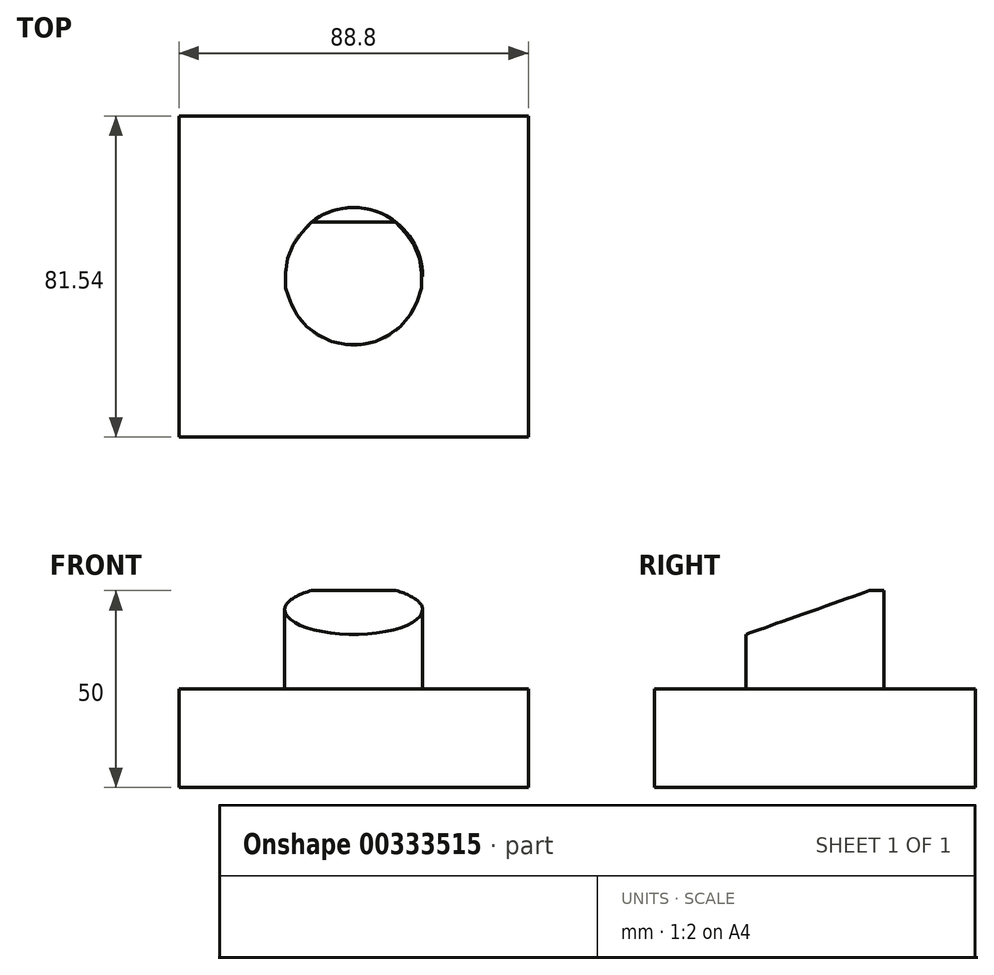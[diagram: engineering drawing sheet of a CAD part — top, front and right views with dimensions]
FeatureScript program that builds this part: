
annotation { "Feature Type Name" : "Feature", "Feature Type Description" : "" }
export const myFeature = defineFeature(function(context is Context, id is Id, definition is map)
    precondition{}
    {
        {
            var Q0;
            Q0=qCreatedBy(makeId("Top.planeOp"),FACE);
            var sketch = newSketch(context, id + "F0", { "sketchPlane" : qUnion([Q0])});
            skLineSegment(sketch, "E0.bottom", {"start": v(-52.21, -36.92) * mm, "end": v(52.21, -36.92) * mm});
            skLineSegment(sketch, "E0.top", {"start": v(-52.21, 36.92) * mm, "end": v(52.21, 36.92) * mm});
            skLineSegment(sketch, "E0.left", {"start": v(-52.21, -36.92) * mm, "end": v(-52.21, 36.92) * mm});
            skLineSegment(sketch, "E0.right", {"start": v(52.21, -36.92) * mm, "end": v(52.21, 36.92) * mm});
            skPoint(sketch, "E0.middle", {"position": v(0, 0) * mm});
            skCircle(sketch, "E1", {"center": v(0, 0) * mm, "radius": 17.54 * mm});
            skSolve(sketch);
        }
        {
            var Q0;
            Q0=makeQuery(id+"F0.imprint","IMPRINT",FACE,{"disambiguationData":[TD([[makeQuery(id+"F0.imprint","IMPRINT",EDGE,{"derivedFrom":sQuery(id+"F0.wireOp",EDGE,"E1")}),1.0]])]});
            extrude(context, id + "F1", {"entities" : qUnion([Q0]), "depth" : 50 * mm, "offsetDistance" : 25 * mm});
        }
        {
            var Q0;
            Q0=qCreatedBy(makeId("Top.planeOp"),FACE);
            var sketch = newSketch(context, id + "F2", { "sketchPlane" : qUnion([Q0])});
            skLineSegment(sketch, "E2.bottom", {"start": v(-44.4, -40.77) * mm, "end": v(44.4, -40.77) * mm});
            skLineSegment(sketch, "E2.top", {"start": v(-44.4, 40.77) * mm, "end": v(44.4, 40.77) * mm});
            skLineSegment(sketch, "E2.left", {"start": v(-44.4, -40.77) * mm, "end": v(-44.4, 40.77) * mm});
            skLineSegment(sketch, "E2.right", {"start": v(44.4, -40.77) * mm, "end": v(44.4, 40.77) * mm});
            skPoint(sketch, "E2.middle", {"position": v(0, 0) * mm});
            skSolve(sketch);
        }
        {
            var Q0;
            Q0=makeQuery(id+"F2.imprint","IMPRINT",FACE,{"disambiguationData":[TD([[makeQuery(id+"F2.imprint","IMPRINT",EDGE,{"derivedFrom":sQuery(id+"F2.wireOp",EDGE,"E2.bottom")}),1.0]])]});
            extrude(context, id + "F3", {"entities" : qUnion([Q0]), "operationType" : NewBodyOperationType.ADD, "depth" : 25 * mm, "offsetDistance" : 25 * mm});
        }
        {
            var Q0;
            Q0=qCreatedBy(makeId("Right.planeOp"),FACE);
            var sketch = newSketch(context, id + "F4", { "sketchPlane" : qUnion([Q0])});
            skLineSegment(sketch, "E3", {"start": v(19.33, 51.92) * mm, "end": v(-20.29, 37.88) * mm});
            skLineSegment(sketch, "E4", {"start": v(-20.29, 53.46) * mm, "end": v(19.33, 51.92) * mm});
            skLineSegment(sketch, "E5", {"start": v(-20.29, 37.88) * mm, "end": v(-20.29, 53.46) * mm});
            skSolve(sketch);
        }
        {
            var Q0;
            Q0=makeQuery(id+"F4.imprint","IMPRINT",FACE,{"disambiguationData":[TD([[makeQuery(id+"F4.imprint","IMPRINT",EDGE,{"derivedFrom":sQuery(id+"F4.wireOp",EDGE,"E3")}),-1.0]])]});
            extrude(context, id + "F5", {"entities" : qUnion([Q0]), "operationType" : NewBodyOperationType.REMOVE, "oppositeDirection" : true, "depth" : 50 * mm, "offsetDistance" : 25 * mm, "symmetric" : true});
        }
    });
